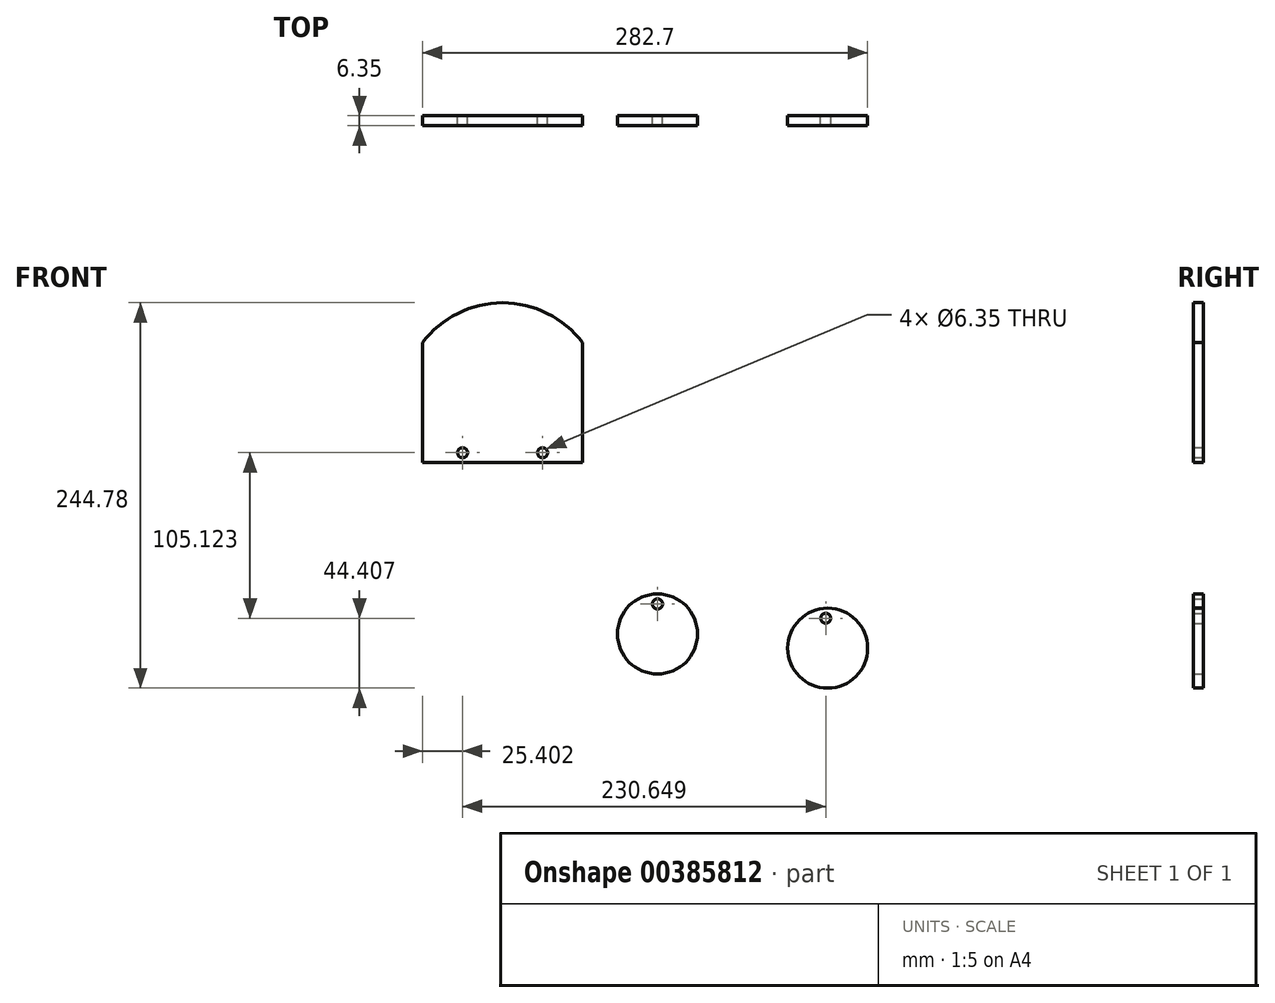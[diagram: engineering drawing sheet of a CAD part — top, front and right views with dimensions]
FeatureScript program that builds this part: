
annotation { "Feature Type Name" : "Feature", "Feature Type Description" : "" }
export const myFeature = defineFeature(function(context is Context, id is Id, definition is map)
    precondition{}
    {
        {
            var Q0;
            Q0=qCreatedBy(makeId("Front.planeOp"),FACE);
            var sketch = newSketch(context, id + "F0", { "sketchPlane" : qUnion([Q0])});
            skCircle(sketch, "E0", {"center": v(-34.44, 10.34) * mm, "radius": 25.4 * mm});
            skLineSegment(sketch, "E1.top", {"start": v(-183.66, 119.1) * mm, "end": v(-82.06, 119.1) * mm});
            skLineSegment(sketch, "E1.left", {"start": v(-183.66, 195.3) * mm, "end": v(-183.66, 119.1) * mm});
            skLineSegment(sketch, "E1.right", {"start": v(-82.06, 195.3) * mm, "end": v(-82.06, 119.1) * mm});
            skCircle(sketch, "E2", {"center": v(73.64, 1.3) * mm, "radius": 25.4 * mm});
            skCircle(sketch, "E3", {"center": v(-158.26, 125.44) * mm, "radius": 3.18 * mm});
            skCircle(sketch, "E4", {"center": v(-34.44, 29.4) * mm, "radius": 3.18 * mm});
            skCircle(sketch, "E5", {"center": v(72.4, 20.32) * mm, "radius": 3.18 * mm});
            skArc(sketch, "E6", {"start": v(-82.06, 195.3) * mm, "mid": v(-132.86, 220.7) * mm, "end": v(-183.66, 195.3) * mm});
            skCircle(sketch, "E7", {"center": v(-107.46, 125.44) * mm, "radius": 3.18 * mm});
            skSolve(sketch);
        }
        {
            var Q0;
            Q0=makeQuery(id+"F0.imprint","IMPRINT",FACE,{"disambiguationData":[TD([[makeQuery(id+"F0.imprint","IMPRINT",EDGE,{"derivedFrom":sQuery(id+"F0.wireOp",EDGE,"E1.top")}),1.0]])]});
            var Q1;
            Q1=makeQuery(id+"F0.imprint","IMPRINT",FACE,{"disambiguationData":[TD([[makeQuery(id+"F0.imprint","IMPRINT",EDGE,{"derivedFrom":sQuery(id+"F0.wireOp",EDGE,"E0")}),1.0]])]});
            var Q2;
            Q2=makeQuery(id+"F0.imprint","IMPRINT",FACE,{"disambiguationData":[TD([[makeQuery(id+"F0.imprint","IMPRINT",EDGE,{"derivedFrom":sQuery(id+"F0.wireOp",EDGE,"E2")}),1.0]])]});
            var Q3;
            Q3=makeQuery(id+"F0.imprint","IMPRINT",FACE,{"disambiguationData":[TD([[makeQuery(id+"F0.imprint","IMPRINT",EDGE,{"derivedFrom":sQuery(id+"F0.wireOp",EDGE,"Rr705ZB9-WNvm-h7yN-g5ON-A9tIXCPgGeZ1")}),1.0]])]});
            extrude(context, id + "F1", {"entities" : qUnion([Q0, Q1, Q2, Q3]), "depth" : 6.35 * mm});
        }
    });
